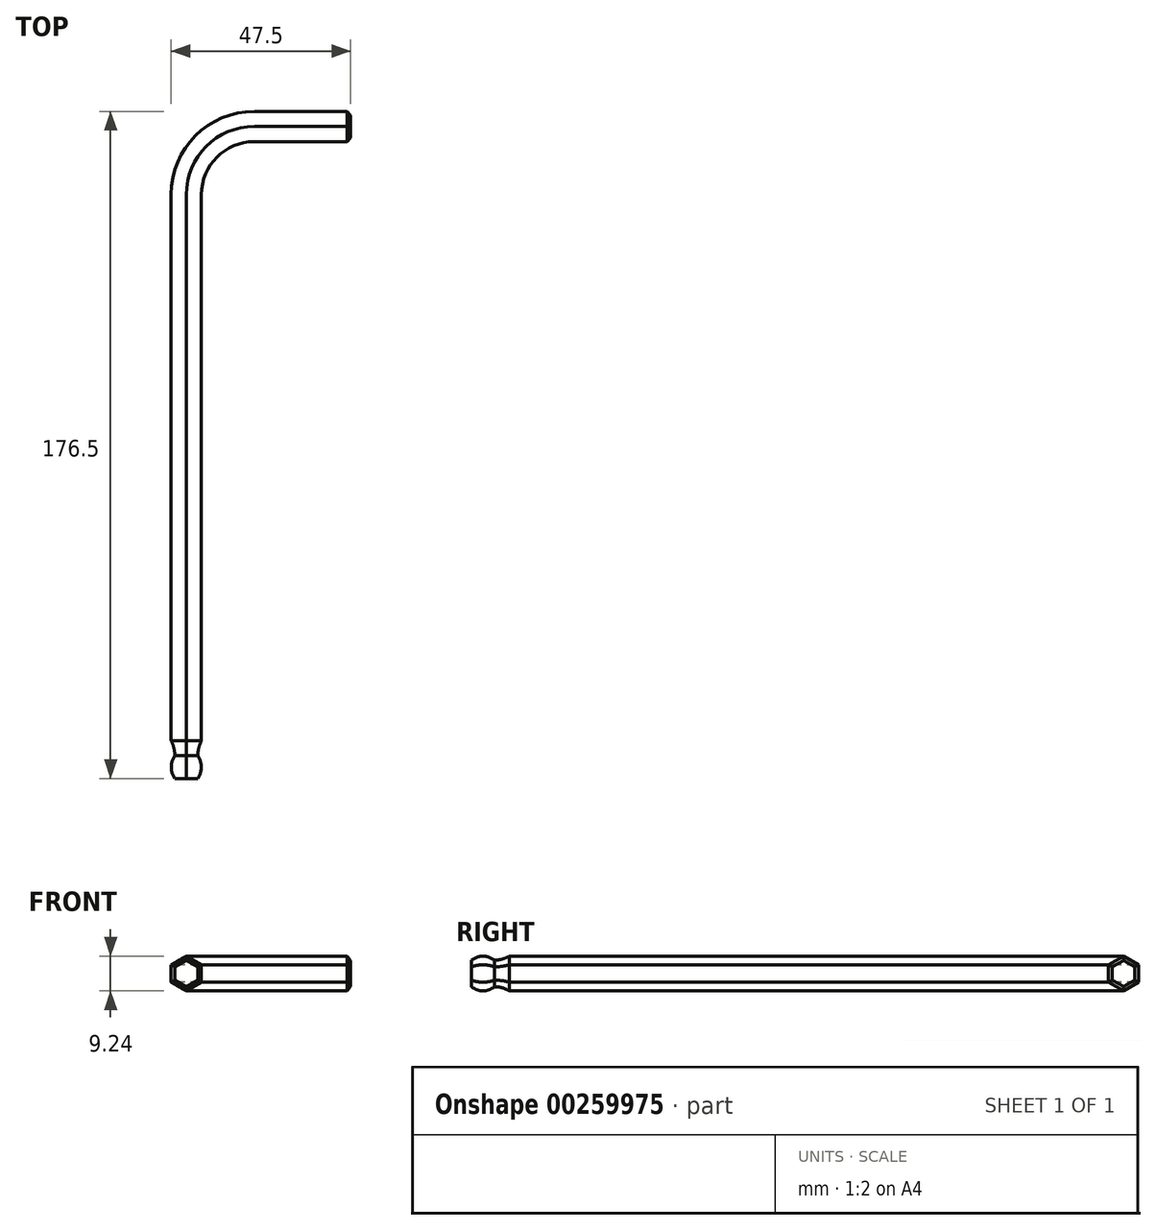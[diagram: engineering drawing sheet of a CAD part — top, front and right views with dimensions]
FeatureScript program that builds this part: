
annotation { "Feature Type Name" : "Feature", "Feature Type Description" : "" }
export const myFeature = defineFeature(function(context is Context, id is Id, definition is map)
    precondition{}
    {
        {
            var Q0;
            Q0=qCreatedBy(makeId("Top.planeOp"),FACE);
            var sketch = newSketch(context, id + "F0", { "sketchPlane" : qUnion([Q0]), "disableImprinting" : false});
            skLineSegment(sketch, "E0", {"start": v(0, 0) * mm, "end": v(0, 154.5) * mm});
            skArc(sketch, "E1", {"start": v(18, 172.5) * mm, "mid": v(5.27, 167.23) * mm, "end": v(0, 154.5) * mm});
            skLineSegment(sketch, "E2", {"start": v(18, 172.5) * mm, "end": v(43.5, 172.5) * mm});
            skSolve(sketch);
        }
        {
            var Q0;
            Q0=qCreatedBy(makeId("Right.planeOp"),FACE);
            cPlane(context, id + "F1", {"entities" : qUnion([Q0]), "cplaneType" : CPlaneType.OFFSET, "offset" : 43.5 * mm, "width" : 150 * mm, "height" : 150 * mm});
        }
        {
            var Q0;
            Q0=qCreatedBy(id+"F1.planeOp",FACE);
            var sketch = newSketch(context, id + "F2", { "sketchPlane" : qUnion([Q0])});
            skCircle(sketch, "E3.cCircle", {"center": v(172.5, 0) * mm, "radius": 4 * mm, "construction": true});
            skLineSegment(sketch, "E3.0", {"start": v(168.5, -2.3) * mm, "end": v(168.5, 2.3) * mm});
            skLineSegment(sketch, "E3.1", {"start": v(168.5, 2.3) * mm, "end": v(172.5, 4.62) * mm});
            skLineSegment(sketch, "E3.2", {"start": v(172.5, 4.62) * mm, "end": v(176.5, 2.3) * mm});
            skLineSegment(sketch, "E3.3", {"start": v(176.5, 2.3) * mm, "end": v(176.5, -2.3) * mm});
            skLineSegment(sketch, "E3.4", {"start": v(176.5, -2.3) * mm, "end": v(172.5, -4.62) * mm});
            skLineSegment(sketch, "E3.5", {"start": v(172.5, -4.62) * mm, "end": v(168.5, -2.3) * mm});
            skPoint(sketch, "E3.0.midPoint", {"position": v(168.5, 0) * mm});
            skSolve(sketch);
        }
        {
            var Q0;
            Q0=makeQuery(id+"F2.imprint","IMPRINT",FACE,{"disambiguationData":[TD([[makeQuery(id+"F2.imprint","IMPRINT",EDGE,{"derivedFrom":sQuery(id+"F2.wireOp",EDGE,"E3.0")}),-1.0]])]});
            var Q1;
            Q1=qConstructionFilter(qBodyType(qCreatedBy(id+"F0",EDGE),BodyType.WIRE),ConstructionObject.NO);
            sweep(context, id + "F3", {"profiles" : qUnion([Q0]), "path" : qUnion([Q1])});
        }
        {
            var Q0;
            Q0=makeQuery(id+"F3.opSweep","CAP_FACE",FACE,{"disambiguationData":[OSD([sQuery(id+"F0.wireOp",VERTEX,"E2.end"),sQuery(id+"F2.wireOp",EDGE,"E3.0"),sQuery(id+"F2.wireOp",EDGE,"E3.1"),sQuery(id+"F2.wireOp",EDGE,"E3.2"),sQuery(id+"F2.wireOp",EDGE,"E3.3"),sQuery(id+"F2.wireOp",EDGE,"E3.4"),sQuery(id+"F2.wireOp",EDGE,"E3.5")])],"isStart":true});
            chamfer(context, id + "F4", {"entities" : qUnion([Q0]), "width" : 1 * mm, "tangentPropagation" : true});
        }
        {
            var Q0;
            Q0=qCreatedBy(makeId("Right.planeOp"),FACE);
            var sketch = newSketch(context, id + "F5", { "sketchPlane" : qUnion([Q0])});
            skArc(sketch, "E4", {"start": v(10, -4.62) * mm, "mid": v(8.07, -3.8) * mm, "end": v(6, -3.5) * mm});
            skArc(sketch, "E5", {"start": v(0, -3.5) * mm, "mid": v(3, -4.6) * mm, "end": v(6, -3.5) * mm});
            skLineSegment(sketch, "E6", {"start": v(10, -4.62) * mm, "end": v(10, -6.5) * mm});
            skLineSegment(sketch, "E7", {"start": v(10, -6.5) * mm, "end": v(0, -6.5) * mm});
            skLineSegment(sketch, "E8", {"start": v(0, -6.5) * mm, "end": v(0, -3.5) * mm});
            skSolve(sketch);
        }
        {
            var Q0;
            Q0=qSketchRegion(id+"F5",true);
            var Q1;
            Q1=makeQuery(id+"F3.opSweep","CAP_EDGE",EDGE,{"disambiguationData":[OSD([sQuery(id+"F0.wireOp",VERTEX,"E0.start"),sQuery(id+"F2.wireOp",EDGE,"E3.4")])],"isStart":false});
            var Q2;
            Q2=makeQuery(id+"F3.opSweep","CAP_EDGE",EDGE,{"disambiguationData":[OSD([sQuery(id+"F0.wireOp",VERTEX,"E0.start"),sQuery(id+"F2.wireOp",EDGE,"E3.3")])],"isStart":false});
            var Q3;
            Q3=makeQuery(id+"F3.opSweep","CAP_EDGE",EDGE,{"disambiguationData":[OSD([sQuery(id+"F0.wireOp",VERTEX,"E0.start"),sQuery(id+"F2.wireOp",EDGE,"E3.2")])],"isStart":false});
            var Q4;
            Q4=makeQuery(id+"F3.opSweep","CAP_EDGE",EDGE,{"disambiguationData":[OSD([sQuery(id+"F0.wireOp",VERTEX,"E0.start"),sQuery(id+"F2.wireOp",EDGE,"E3.1")])],"isStart":false});
            var Q5;
            Q5=makeQuery(id+"F3.opSweep","CAP_EDGE",EDGE,{"disambiguationData":[OSD([sQuery(id+"F0.wireOp",VERTEX,"E0.start"),sQuery(id+"F2.wireOp",EDGE,"E3.0")])],"isStart":false});
            var Q6;
            Q6=makeQuery(id+"F3.opSweep","CAP_EDGE",EDGE,{"disambiguationData":[OSD([sQuery(id+"F0.wireOp",VERTEX,"E0.start"),sQuery(id+"F2.wireOp",EDGE,"E3.5")])],"isStart":false});
            sweep(context, id + "F6", {"operationType" : NewBodyOperationType.REMOVE, "profiles" : qUnion([Q0]), "path" : qUnion([Q1, Q2, Q3, Q4, Q5, Q6])});
        }
    });
